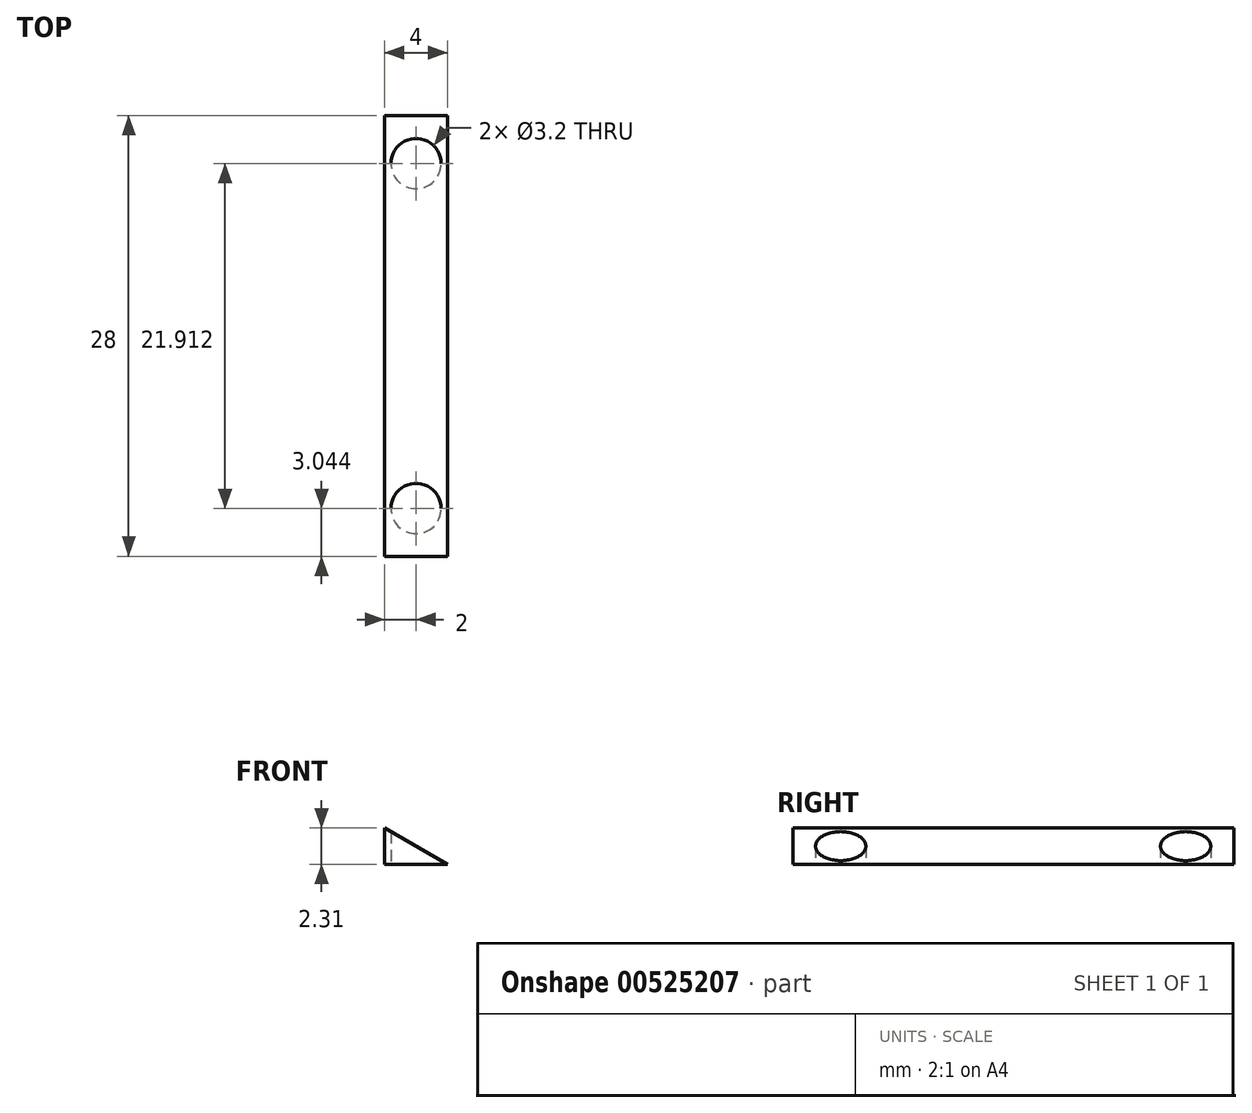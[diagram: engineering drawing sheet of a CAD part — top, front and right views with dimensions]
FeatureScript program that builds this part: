
annotation { "Feature Type Name" : "Feature", "Feature Type Description" : "" }
export const myFeature = defineFeature(function(context is Context, id is Id, definition is map)
    precondition{}
    {
        {
            var Q0;
            Q0=qCreatedBy(makeId("Front.planeOp"),FACE);
            var sketch = newSketch(context, id + "F0", { "sketchPlane" : qUnion([Q0])});
            skLineSegment(sketch, "E0", {"start": v(0, 0) * mm, "end": v(0, 2.3) * mm});
            skLineSegment(sketch, "E1", {"start": v(0, 2.3) * mm, "end": v(4, 0) * mm});
            skLineSegment(sketch, "E2", {"start": v(4, 0) * mm, "end": v(0, 0) * mm});
            skSolve(sketch);
        }
        {
            var Q0;
            Q0 = qSketchRegion(id + "F0", true);
            extrude(context, id + "F1", {"entities" : qUnion([Q0]), "depth" : 28 * mm, "offsetDistance" : 25 * mm});
        }
        {
            var Q0;
            Q0=makeQuery(id+"F1.opExtrude","SWEPT_FACE",FACE,{"disambiguationData":[OSD([sQuery(id+"F0.wireOp",EDGE,"E2")])]});
            var sketch = newSketch(context, id + "F2", { "sketchPlane" : qUnion([Q0])});
            skLineSegment(sketch, "E3", {"start": v(4, 14) * mm, "end": v(3.3, 14) * mm});
            skPoint(sketch, "E4", {"position": v(2, 24.96) * mm});
            skPoint(sketch, "E4.positionSnap0", {"position": v(2, 28) * mm});
            skCircle(sketch, "E5", {"center": v(2, 24.96) * mm, "radius": 1.6 * mm});
            skCircle(sketch, "E6.MirrorC", {"center": v(2, 3.04) * mm, "radius": 1.6 * mm});
            skSolve(sketch);
        }
        {
            var Q0;
            Q0=sQuery(id+"F2.wireOp",VERTEX,"E4");
            var Q1;
            Q1=makeQuery(id+"F1.opExtrude","SWEPT_BODY",BODY,{"disambiguationData":[OSD([sQuery(id+"F0.wireOp",EDGE,"E0"),sQuery(id+"F0.wireOp",EDGE,"E1"),sQuery(id+"F0.wireOp",EDGE,"E2")])]});
            hole(context, id + "F3", {"style" : HoleStyle.SIMPLE, "endStyle" : HoleEndStyle.BLIND, "holeDiameter" : 3 * mm, "holeDepth" : 14.4 * mm, "isTappedThrough" : true, "tappedDepth" : 12 * mm, "tapClearance" : 3, "locations" : qUnion([Q0]), "scope" : qUnion([Q1])});
        }
        {
            var Q0;
            Q0 = qSketchRegion(id + "F2", true);
            extrude(context, id + "F4", {"entities" : qUnion([Q0]), "operationType" : NewBodyOperationType.REMOVE, "oppositeDirection" : true, "depth" : 25 * mm, "offsetDistance" : 25 * mm});
        }
    });
